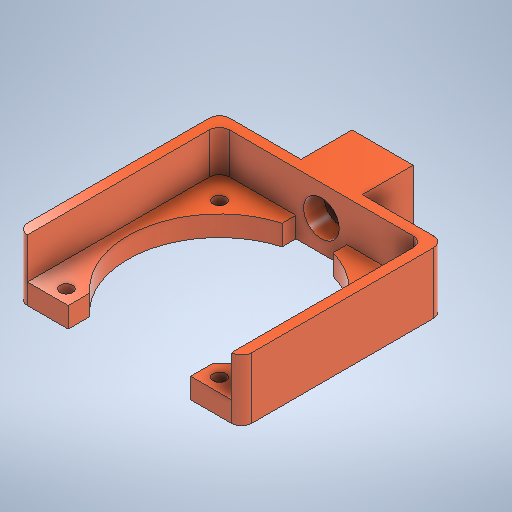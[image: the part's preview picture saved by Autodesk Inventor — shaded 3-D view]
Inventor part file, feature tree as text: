
AUTODESK INVENTOR PART (.ipt)
format: ipt  version: 2025 (Build 290162010, 162A)  size: 394,752 bytes
history: native  units: mm
features: extrude x6, sketch x6, fillet x1
ambient origin geometry x8: Origin, YZ Plane, XZ Plane, XY Plane, X Axis, Y Axis, Z Axis, Center Point
bodies: Solid1 (feature_tree)
feature tree (13):
  extrude  "Extrusion1"  Depth=38.0mm
  extrude  "Extrusion2"  Depth=4.0mm
  extrude  "Extrusion3"  Depth=4.0mm
  fillet  "Fillet2"  Radius=2.5mm
  extrude  "Extrusion4"  Depth=2.5mm
  extrude  "Extrusion5"  Depth=36.0mm
  extrude  "Extrusion6"  Depth=40.0mm
  sketch  "Sketch1"  dims[d0=38.0mm d1=38.0mm]
  sketch  "Sketch2"  dims[d2=4.0mm d3=4.0mm]
  sketch  "Sketch3"  dims[d4=4.0mm d5=4.0mm d6=2.5mm]
  sketch  "Sketch4"  dims[d7=2.5mm d8=2.5mm]
  sketch  "Sketch5"  dims[d9=2.5mm d10=36.0mm]
  sketch  "Sketch6"  dims[d11=40.0mm d12=40.0mm d13=44.0mm d14=44.0mm d15=10.0mm d16=10.0mm d17=17.0mm d18=17.0mm d19=18.0mm d20=18.0mm d21=4.0mm d22=0.0mm d23=2.0mm d24=8.0mm d25=40.0mm d26=40.0mm d27=40.0mm d28=90.0deg d29=8.0mm d30=0.0mm d32=0.0mm d33=0.0mm d34=2.0mm d35=12.0mm d36=12.0mm d37=6.0mm d38=10.0mm d39=0.0mm d40=7.0mm d41=6.0mm d42=22.0mm d43=4.0mm d44=0.0mm d45=4.0mm d46=6.0mm d47=22.0mm d48=5.0mm d49=0.0mm d50=0.5mm d51=0.872665mm d52=0.5mm d53=0.872665mm]
